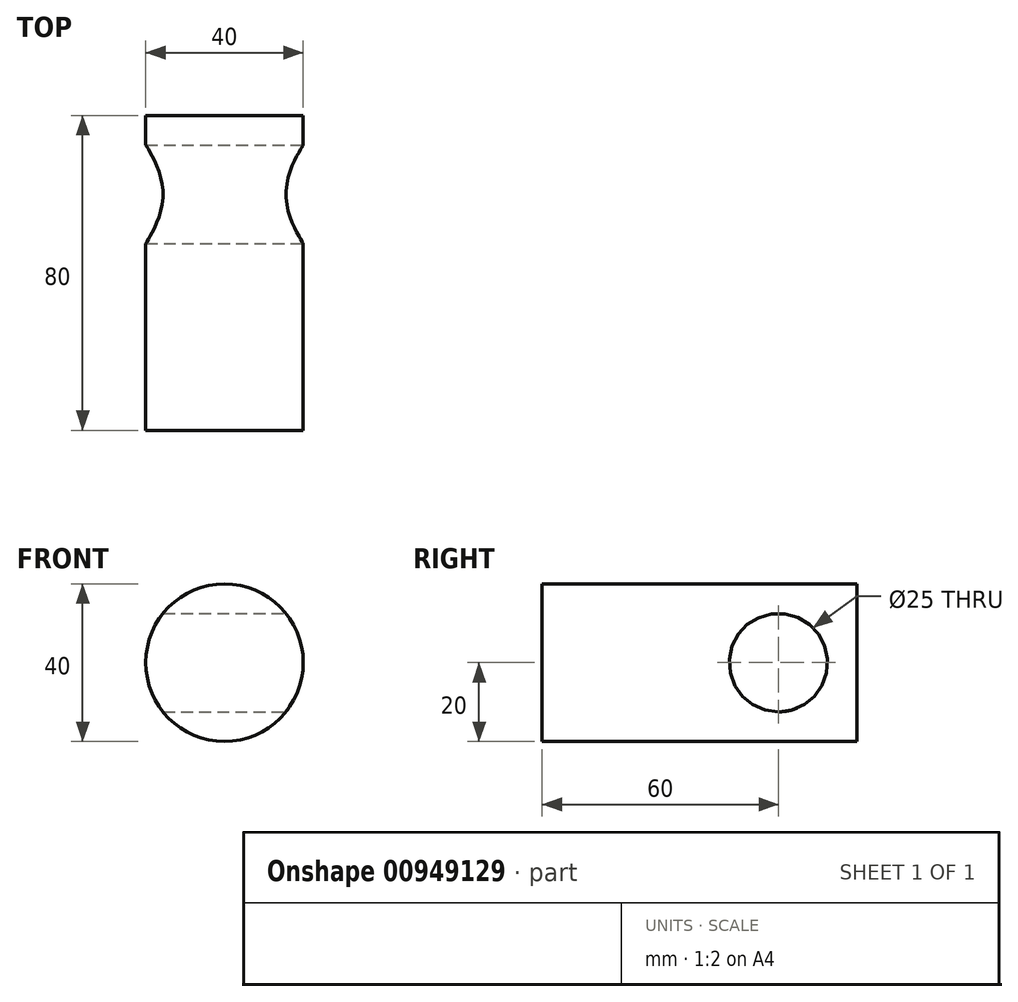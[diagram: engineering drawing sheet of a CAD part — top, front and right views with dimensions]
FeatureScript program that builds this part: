
annotation { "Feature Type Name" : "Feature", "Feature Type Description" : "" }
export const myFeature = defineFeature(function(context is Context, id is Id, definition is map)
    precondition{}
    {
        {
            var Q0;
            Q0=qCreatedBy(makeId("Front.planeOp"),FACE);
            var sketch = newSketch(context, id + "F0", { "sketchPlane" : qUnion([Q0])});
            skCircle(sketch, "E0", {"center": v(0, 0) * mm, "radius": 20 * mm});
            skSolve(sketch);
        }
        {
            var Q0;
            Q0=makeQuery(id+"F0.imprint","IMPRINT",FACE,{"disambiguationData":[TD([[makeQuery(id+"F0.imprint","IMPRINT",EDGE,{"derivedFrom":sQuery(id+"F0.wireOp",EDGE,"E0")}),1.0]])]});
            extrude(context, id + "F1", {"entities" : qUnion([Q0]), "endBound" : BoundingType.SYMMETRIC, "depth" : 120 * mm, "offsetDistance" : 25.4 * mm});
        }
        {
            var Q0;
            Q0=qCreatedBy(makeId("Right.planeOp"),FACE);
            var sketch = newSketch(context, id + "F2", { "sketchPlane" : qUnion([Q0])});
            skCircle(sketch, "E1", {"center": v(0, 0) * mm, "radius": 12.5 * mm});
            skSolve(sketch);
        }
        {
            var Q0;
            Q0=makeQuery(id+"F2.imprint","IMPRINT",FACE,{"disambiguationData":[TD([[makeQuery(id+"F2.imprint","IMPRINT",EDGE,{"derivedFrom":sQuery(id+"F2.wireOp",EDGE,"E1")}),1.0]])]});
            extrude(context, id + "F3", {"entities" : qUnion([Q0]), "operationType" : NewBodyOperationType.REMOVE, "endBound" : BoundingType.SYMMETRIC, "oppositeDirection" : true, "depth" : 40 * mm, "offsetDistance" : 25.4 * mm});
        }
        {
            var Q0;
            Q0=makeQuery(id+"F1.opExtrude","CAP_FACE",FACE,{"disambiguationData":[OSD([sQuery(id+"F0.wireOp",EDGE,"E0")])],"isStart":true});
            extrude(context, id + "F4", {"entities" : qUnion([Q0]), "operationType" : NewBodyOperationType.REMOVE, "endBound" : BoundingType.SYMMETRIC, "oppositeDirection" : true, "depth" : 40 * mm, "offsetDistance" : 25.4 * mm});
        }
        {
            var Q0;
            Q0=makeQuery(id+"F4.boolean.opBoolean","COPY",FACE,{"derivedFrom":makeQuery(id+"F4.opExtrude","CAP_FACE",FACE,{"disambiguationData":[OSD([sQuery(id+"F0.wireOp",EDGE,"E0")])],"isStart":false})});
            extrude(context, id + "F5", {"entities" : qUnion([Q0]), "operationType" : NewBodyOperationType.REMOVE, "endBound" : BoundingType.SYMMETRIC, "oppositeDirection" : true, "depth" : 40 * mm, "offsetDistance" : 25.4 * mm});
        }
    });
